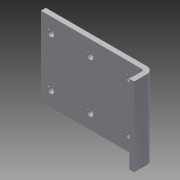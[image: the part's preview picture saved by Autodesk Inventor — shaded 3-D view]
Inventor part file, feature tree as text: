
AUTODESK INVENTOR PART (.ipt)
format: ipt  version: 2014 (Build 180170000, 170)  size: 111,104 bytes
history: native  units: in
note: dims shown in document units (in); Inventor stores cm internally (conversion verified against a paired STEP export)
features: sheet_metal_op x4, sketch x2, other x2
ambient origin geometry x8: Origin, YZ Plane, XZ Plane, XY Plane, X Axis, Y Axis, Z Axis, Center Point
bodies: Solid1 (feature_tree)
feature tree (8):
  sheet_metal_op  "Face1"
  sheet_metal_op  "Flange1"
  sketch  "Sketch1"  dims[d1=1.1811in d3=0.7874in d4=2.0in d5=2.75in d6=0.163in d7=0.25in d8=0.375in d9=1.0in d10=1.25in]
  other  "Plate1"
  sketch  "Sketch2"  dims[d11=0.125in d12=0.125in d13=0.0625in d14=0.25in d15=0.125in d16=0.5in d17=90.0deg d18=0.05in d19=0.5in d20=0.125in d21=0.125in]
  other  "Plate2"
  sheet_metal_op  "Bend1"
  sheet_metal_op  "Corner1"
